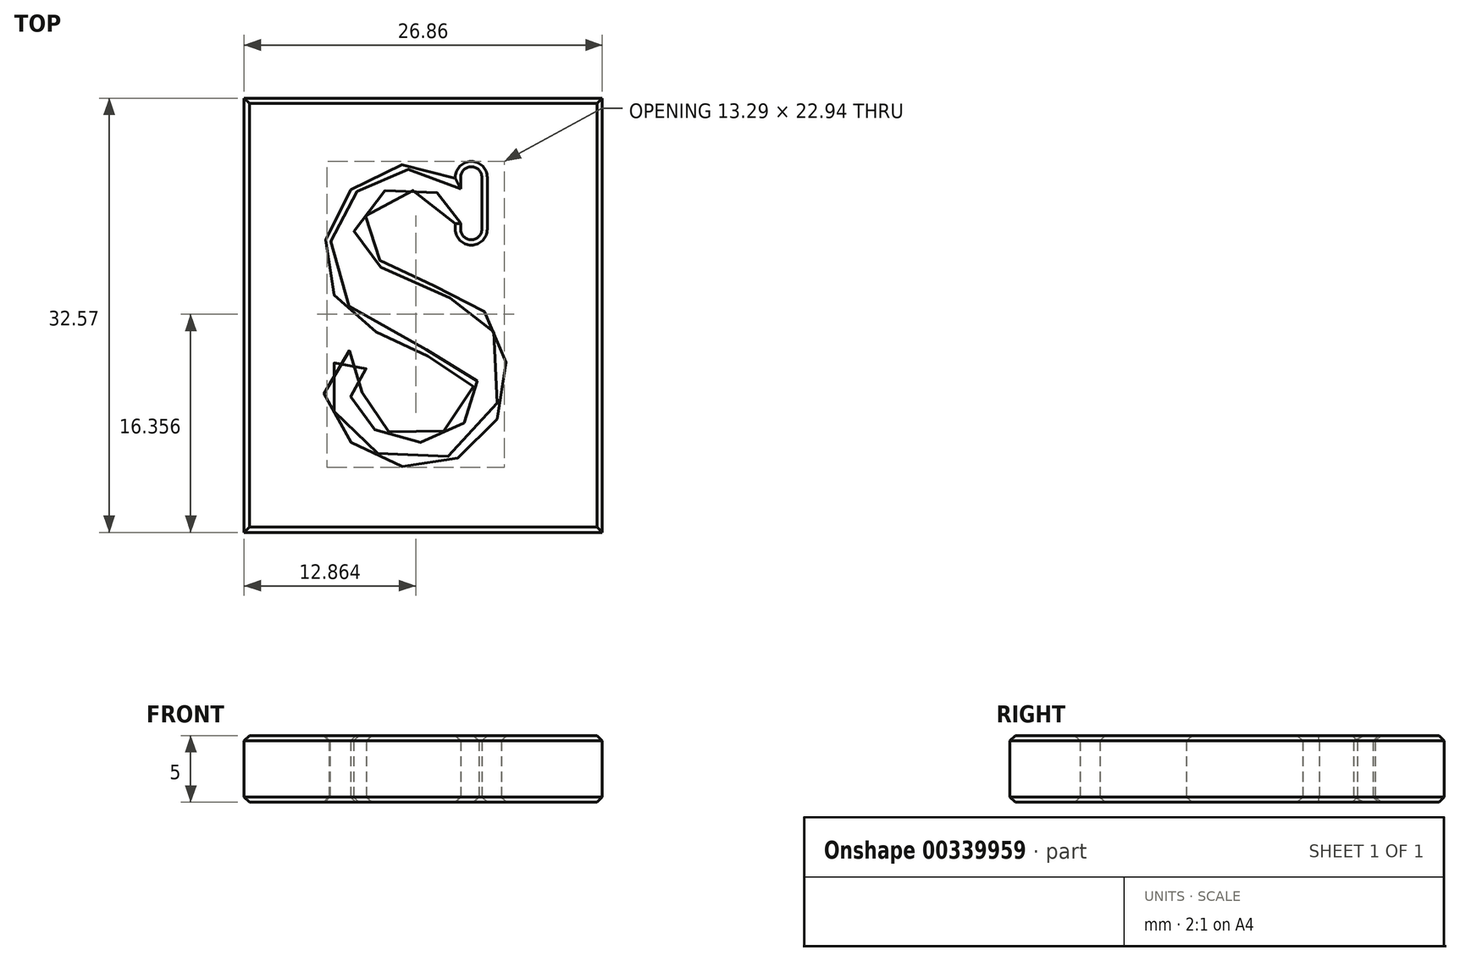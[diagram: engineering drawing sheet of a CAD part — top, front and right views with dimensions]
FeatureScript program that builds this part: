
annotation { "Feature Type Name" : "Feature", "Feature Type Description" : "" }
export const myFeature = defineFeature(function(context is Context, id is Id, definition is map)
    precondition{}
    {
        {
            var Q0;
            Q0=qCreatedBy(makeId("Top.planeOp"),FACE);
            var sketch = newSketch(context, id + "F0", { "sketchPlane" : qUnion([Q0])});
            skLineSegment(sketch, "E0.bottom", {"start": v(2.8, 12.73) * mm, "end": v(4.4, 12.73) * mm});
            skLineSegment(sketch, "E0.top", {"start": v(2.8, 7.25) * mm, "end": v(4.4, 7.25) * mm});
            skLineSegment(sketch, "E0.left", {"start": v(2.8, 12.73) * mm, "end": v(2.8, 7.25) * mm});
            skLineSegment(sketch, "E0.right", {"start": v(4.4, 12.73) * mm, "end": v(4.4, 7.25) * mm});
            skFitSpline(sketch, "E1", {"points": [v(2.8, 11.07) * mm, v(-0.9, 12.54) * mm, v(-4.66, 11.14) * mm, v(-6.76, 7.88) * mm, v(-5.79, 2.53) * mm, v(2.32, -1.93) * mm, v(4.16, -3.78) * mm, v(3.22, -6.3) * mm, v(0.7, -7.81) * mm, v(-2.21, -7.72) * mm, v(-4.61, -6.15) * mm, v(-5.44, -4.5) * mm, v(-4.63, -3.7) * mm, v(-4.42, -2.12) * mm, v(-6.18, -1.54) * mm, v(-7.07, -3.65) * mm, v(-5.85, -6.95) * mm, v(-0.94, -9.42) * mm, v(4.85, -6.65) * mm, v(5.42, 0) * mm, v(2.92, 2.43) * mm, v(-3.42, 5.33) * mm, v(-5.22, 7.36) * mm, v(-3.9, 10.19) * mm, v(-0.72, 11.34) * mm, v(2.23, 9.88) * mm, v(2.8, 8.48) * mm], "startDerivative": vector(-82.04, 68.37) * mm, "endDerivative": vector(9.55, -56.26) * mm});
            skLineSegment(sketch, "E2.bottom", {"start": v(-13.43, 17.87) * mm, "end": v(13.43, 17.87) * mm});
            skLineSegment(sketch, "E2.top", {"start": v(-13.43, -14.7) * mm, "end": v(13.43, -14.7) * mm});
            skLineSegment(sketch, "E2.left", {"start": v(-13.43, 17.87) * mm, "end": v(-13.43, -14.7) * mm});
            skLineSegment(sketch, "E2.right", {"start": v(13.43, 17.87) * mm, "end": v(13.43, -14.7) * mm});
            skPoint(sketch, "E2.middle", {"position": v(0, 1.58) * mm});
            skSolve(sketch);
        }
        {
            var Q0;
            Q0=qSketchRegion(id+"F0",true);
            extrude(context, id + "F1", {"entities" : qUnion([Q0]), "depth" : 4 * mm});
        }
        {
            var Q0;
            Q0 = qSketchRegion(id + "F0", true);
            extrude(context, id + "F2", {"entities" : qUnion([Q0]), "operationType" : NewBodyOperationType.ADD, "depth" : 5 * mm});
        }
        {
            var Q0;
            {var subQ0=sQuery(id+"F0.wireOp",EDGE,"E0.right");var subQ1=sQuery(id+"F0.wireOp",EDGE,"E0.bottom");Q0=makeQuery(id+"F2.boolean.opBoolean","MERGE",EDGE,{"derivedFrom":[makeQuery(id+"F1.opExtrude","SWEPT_EDGE",EDGE,{"disambiguationData":[OSD([subQ1,subQ0])]}),makeQuery(id+"F2.opExtrude","SWEPT_EDGE",EDGE,{"disambiguationData":[OSD([subQ1,subQ0])]})]});}
            var Q1;
            {var subQ0=sQuery(id+"F0.wireOp",EDGE,"E0.left");var subQ1=sQuery(id+"F0.wireOp",EDGE,"E0.bottom");Q1=makeQuery(id+"F2.boolean.opBoolean","MERGE",EDGE,{"derivedFrom":[makeQuery(id+"F1.opExtrude","SWEPT_EDGE",EDGE,{"disambiguationData":[OSD([subQ1,subQ0])]}),makeQuery(id+"F2.opExtrude","SWEPT_EDGE",EDGE,{"disambiguationData":[OSD([subQ1,subQ0])]})]});}
            var Q2;
            {var subQ0=sQuery(id+"F0.wireOp",EDGE,"E0.right");var subQ1=sQuery(id+"F0.wireOp",EDGE,"E0.top");Q2=makeQuery(id+"F2.boolean.opBoolean","MERGE",EDGE,{"derivedFrom":[makeQuery(id+"F1.opExtrude","SWEPT_EDGE",EDGE,{"disambiguationData":[OSD([subQ1,subQ0])]}),makeQuery(id+"F2.opExtrude","SWEPT_EDGE",EDGE,{"disambiguationData":[OSD([subQ1,subQ0])]})]});}
            var Q3;
            {var subQ0=sQuery(id+"F0.wireOp",EDGE,"E0.left");var subQ1=sQuery(id+"F0.wireOp",EDGE,"E0.top");Q3=makeQuery(id+"F2.boolean.opBoolean","MERGE",EDGE,{"derivedFrom":[makeQuery(id+"F1.opExtrude","SWEPT_EDGE",EDGE,{"disambiguationData":[OSD([subQ1,subQ0])]}),makeQuery(id+"F2.opExtrude","SWEPT_EDGE",EDGE,{"disambiguationData":[OSD([subQ1,subQ0])]})]});}
            fillet(context, id + "F3", {"entities" : qUnion([Q0, Q1, Q2, Q3]), "radius" : 0.8 * mm, "tangentPropagation" : true, "allowEdgeOverflow" : false});
        }
        {
            var Q0;
            Q0=makeQuery(id+"F2.opExtrude","CAP_FACE",FACE,{"disambiguationData":[OSD([sQuery(id+"F0.wireOp",EDGE,"E0.bottom"),sQuery(id+"F0.wireOp",EDGE,"E0.top"),sQuery(id+"F0.wireOp",EDGE,"E0.left"),sQuery(id+"F0.wireOp",EDGE,"E0.right"),sQuery(id+"F0.wireOp",EDGE,"E1"),sQuery(id+"F0.wireOp",EDGE,"E2.bottom"),sQuery(id+"F0.wireOp",EDGE,"E2.top"),sQuery(id+"F0.wireOp",EDGE,"E2.left"),sQuery(id+"F0.wireOp",EDGE,"E2.right")])],"isStart":false});
            var Q1;
            Q1=makeQuery(id+"F1.opExtrude","CAP_FACE",FACE,{"disambiguationData":[OSD([sQuery(id+"F0.wireOp",EDGE,"E0.bottom"),sQuery(id+"F0.wireOp",EDGE,"E0.top"),sQuery(id+"F0.wireOp",EDGE,"E0.left"),sQuery(id+"F0.wireOp",EDGE,"E0.right"),sQuery(id+"F0.wireOp",EDGE,"E1"),sQuery(id+"F0.wireOp",EDGE,"E2.bottom"),sQuery(id+"F0.wireOp",EDGE,"E2.top"),sQuery(id+"F0.wireOp",EDGE,"E2.left"),sQuery(id+"F0.wireOp",EDGE,"E2.right")])],"isStart":true});
            chamfer(context, id + "F4", {"entities" : qUnion([Q0, Q1]), "width" : 0.4 * mm, "tangentPropagation" : true});
        }
    });
